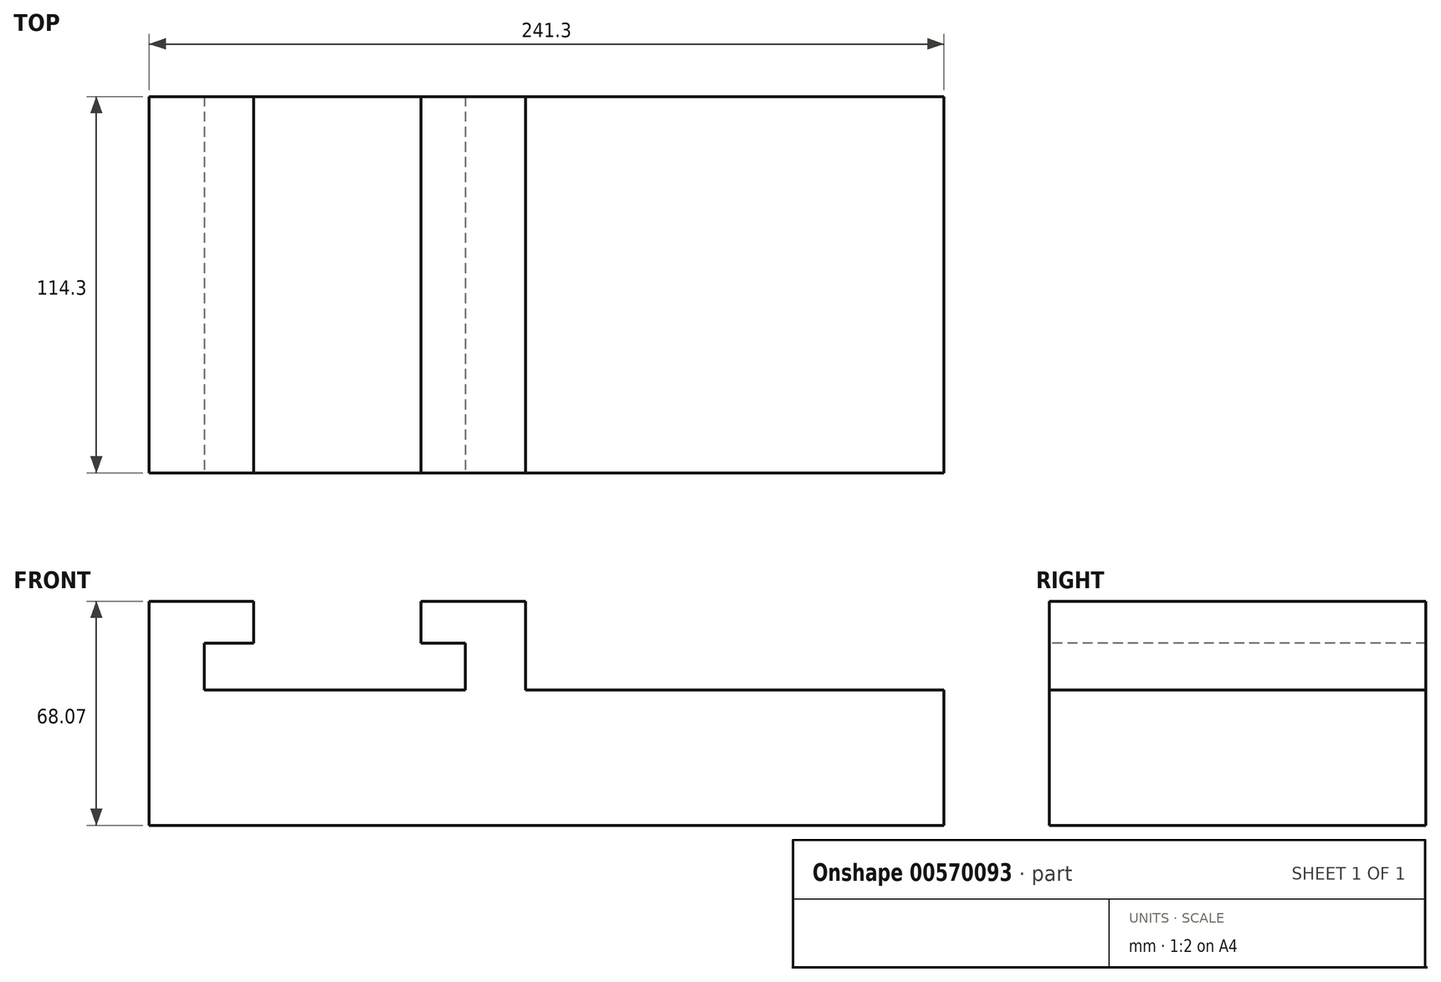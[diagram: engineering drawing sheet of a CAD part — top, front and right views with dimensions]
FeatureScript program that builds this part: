
annotation { "Feature Type Name" : "Feature", "Feature Type Description" : "" }
export const myFeature = defineFeature(function(context is Context, id is Id, definition is map)
    precondition{}
    {
        {
            var Q0;
            Q0=qCreatedBy(makeId("Front.planeOp"),FACE);
            var sketch = newSketch(context, id + "F0", { "sketchPlane" : qUnion([Q0])});
            skLineSegment(sketch, "E0", {"start": v(0, 163.54) * mm, "end": v(0, -163.54) * mm, "construction": true});
            skLineSegment(sketch, "E1", {"start": v(205.78, 0) * mm, "end": v(-205.78, 0) * mm, "construction": true});
            skPoint(sketch, "E2", {"position": v(0, 0) * mm});
            skLineSegment(sketch, "E3", {"start": v(-77.58, 0) * mm, "end": v(-77.58, 68.07) * mm});
            skLineSegment(sketch, "E4", {"start": v(-77.58, 68.07) * mm, "end": v(-45.83, 68.07) * mm});
            skLineSegment(sketch, "E5", {"start": v(-45.83, 68.07) * mm, "end": v(-45.83, 55.37) * mm});
            skLineSegment(sketch, "E6", {"start": v(-45.83, 55.37) * mm, "end": v(-60.8, 55.37) * mm});
            skLineSegment(sketch, "E7", {"start": v(-60.8, 55.37) * mm, "end": v(-60.8, 41.15) * mm});
            skLineSegment(sketch, "E8", {"start": v(-60.8, 41.15) * mm, "end": v(18.44, 41.15) * mm});
            skLineSegment(sketch, "E9", {"start": v(18.44, 41.15) * mm, "end": v(18.44, 55.37) * mm});
            skLineSegment(sketch, "E10", {"start": v(18.44, 55.37) * mm, "end": v(4.97, 55.37) * mm});
            skLineSegment(sketch, "E11", {"start": v(4.97, 55.37) * mm, "end": v(4.97, 68.07) * mm});
            skLineSegment(sketch, "E12", {"start": v(4.97, 68.07) * mm, "end": v(36.72, 68.07) * mm});
            skLineSegment(sketch, "E13", {"start": v(36.72, 68.07) * mm, "end": v(36.72, 41.15) * mm});
            skLineSegment(sketch, "E14", {"start": v(36.72, 41.15) * mm, "end": v(163.72, 41.15) * mm});
            skLineSegment(sketch, "E15", {"start": v(163.72, 41.15) * mm, "end": v(163.72, 0) * mm});
            skLineSegment(sketch, "E16", {"start": v(163.72, 0) * mm, "end": v(-77.58, 0) * mm});
            skSolve(sketch);
        }
        {
            var Q0;
            Q0 = qSketchRegion(id + "F0", true);
            extrude(context, id + "F1", {"entities" : qUnion([Q0]), "oppositeDirection" : true, "depth" : 114.3 * mm, "offsetDistance" : 25.4 * mm});
        }
    });
